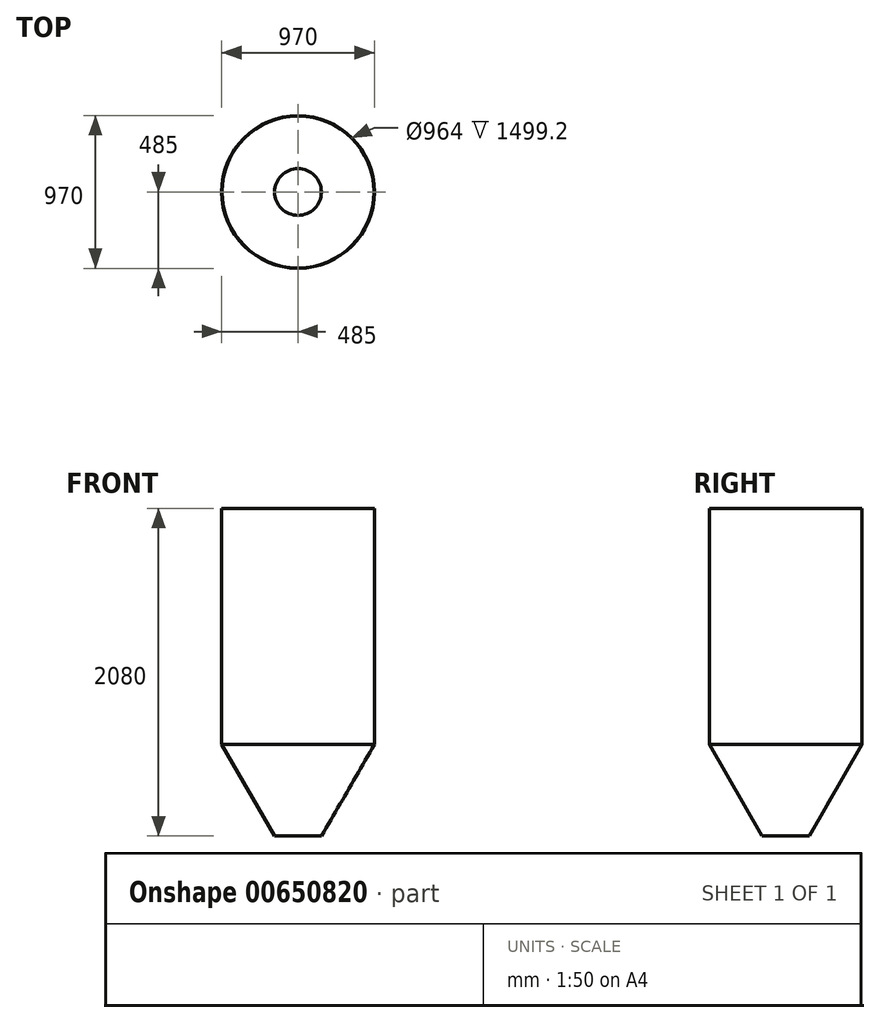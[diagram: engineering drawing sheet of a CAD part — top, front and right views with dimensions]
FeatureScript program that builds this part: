
annotation { "Feature Type Name" : "Feature", "Feature Type Description" : "" }
export const myFeature = defineFeature(function(context is Context, id is Id, definition is map)
    precondition{}
    {
        {
            var Q0;
            Q0=qCreatedBy(makeId("Top.planeOp"),FACE);
            var sketch = newSketch(context, id + "F0", { "sketchPlane" : qUnion([Q0])});
            skCircle(sketch, "E0", {"center": v(0, 0) * mm, "radius": 485 * mm});
            skSolve(sketch);
        }
        {
            var Q0;
            Q0 = qSketchRegion(id + "F0", true);
            extrude(context, id + "F1", {"entities" : qUnion([Q0]), "depth" : 1500 * mm, "offsetDistance" : 25 * mm, "hasSecondDirection" : true, "secondDirectionOppositeDirection" : true, "secondDirectionDepth" : 580 * mm, "hasSecondDirectionDraft" : true, "secondDirectionDraftAngle" : 30 * degree, "secondDirectionDraftPullDirection" : true});
        }
        {
            var Q0;
            Q0=makeQuery(id+"F1.opExtrude","CAP_FACE",FACE,{"disambiguationData":[OSD([sQuery(id+"F0.wireOp",EDGE,"E0")])],"isStart":false});
            shell(context, id + "F2", {"entities" : qUnion([Q0]), "thickness" : 3 * mm});
        }
    });
